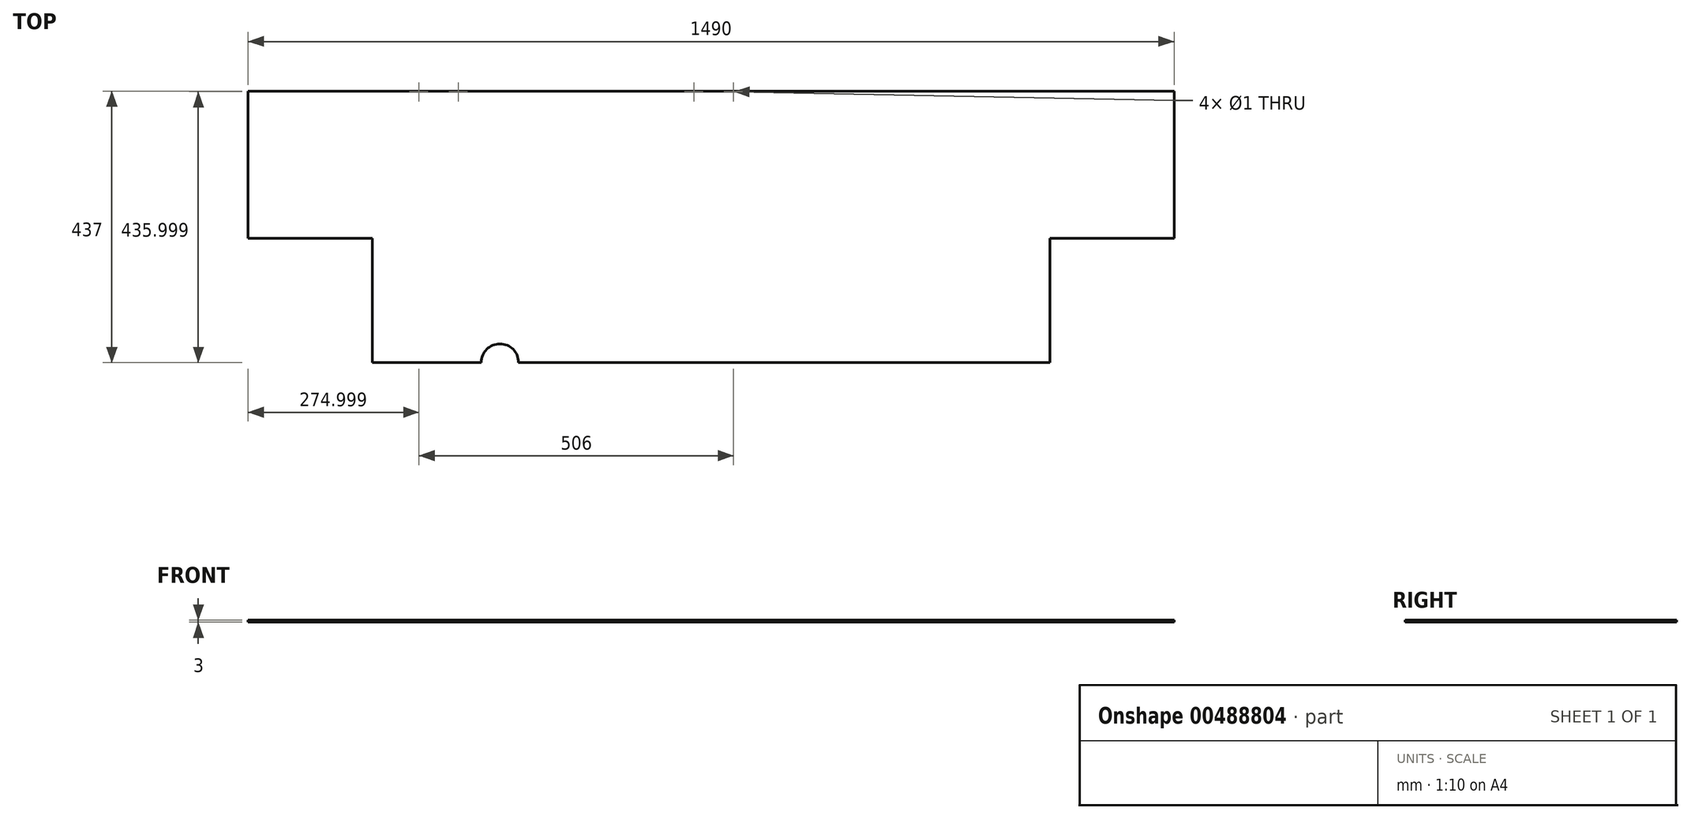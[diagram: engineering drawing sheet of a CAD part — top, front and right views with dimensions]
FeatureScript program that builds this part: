
annotation { "Feature Type Name" : "Feature", "Feature Type Description" : "" }
export const myFeature = defineFeature(function(context is Context, id is Id, definition is map)
    precondition{}
    {
        {
            var Q0;
            Q0=qCreatedBy(makeId("Top.planeOp"),FACE);
            var sketch = newSketch(context, id + "F0", { "sketchPlane" : qUnion([Q0])});
            skLineSegment(sketch, "E0.bottom", {"start": v(-755.66, 172.25) * mm, "end": v(734.34, 172.25) * mm});
            skLineSegment(sketch, "E0.top", {"start": v(-555.66, -264.75) * mm, "end": v(534.34, -264.75) * mm});
            skLineSegment(sketch, "E0.left", {"start": v(-755.66, 172.25) * mm, "end": v(-755.66, -64.75) * mm});
            skLineSegment(sketch, "E0.right", {"start": v(734.34, 172.25) * mm, "end": v(734.34, -64.75) * mm});
            skLineSegment(sketch, "E1.top", {"start": v(-755.66, -64.75) * mm, "end": v(-555.66, -64.75) * mm});
            skLineSegment(sketch, "E1.right", {"start": v(-555.66, -264.75) * mm, "end": v(-555.66, -64.75) * mm});
            skLineSegment(sketch, "E2.top", {"start": v(734.34, -64.75) * mm, "end": v(534.34, -64.75) * mm});
            skLineSegment(sketch, "E2.right", {"start": v(534.34, -264.75) * mm, "end": v(534.34, -64.75) * mm});
            skArc(sketch, "E3", {"start": v(-320.66, -264.75) * mm, "mid": v(-350.66, -234.75) * mm, "end": v(-380.66, -264.75) * mm});
            skLineSegment(sketch, "E4", {"start": v(-755.66, 172.25) * mm, "end": v(-480.66, 172.25) * mm});
            skLineSegment(sketch, "E5", {"start": v(-480.66, 172.25) * mm, "end": v(-402.51, 172.25) * mm});
            skLineSegment(sketch, "E6", {"start": v(-480.66, 172.25) * mm, "end": v(-417.16, 172.25) * mm});
            skLineSegment(sketch, "E7", {"start": v(-417.16, 172.25) * mm, "end": v(-38.16, 172.25) * mm});
            skLineSegment(sketch, "E8", {"start": v(-38.16, 172.25) * mm, "end": v(25.34, 172.25) * mm});
            skLineSegment(sketch, "E9", {"start": v(-480.66, 172.25) * mm, "end": v(-480.66, 170.81) * mm});
            skCircle(sketch, "E10", {"center": v(-480.66, 171.25) * mm, "radius": 0.5 * mm});
            skLineSegment(sketch, "E11", {"start": v(-417.16, 172.25) * mm, "end": v(-417.16, 170.25) * mm});
            skCircle(sketch, "E12", {"center": v(-417.16, 171.25) * mm, "radius": 0.5 * mm});
            skLineSegment(sketch, "E13", {"start": v(-38.16, 172.25) * mm, "end": v(-38.16, 169.8) * mm});
            skCircle(sketch, "E14", {"center": v(-38.16, 171.25) * mm, "radius": 0.5 * mm});
            skLineSegment(sketch, "E15", {"start": v(25.34, 172.25) * mm, "end": v(25.34, 170.25) * mm});
            skCircle(sketch, "E16", {"center": v(25.34, 171.25) * mm, "radius": 0.5 * mm});
            skSolve(sketch);
        }
        {
            var Q0;
            Q0=makeQuery(id+"F0.imprint","IMPRINT",FACE,{"disambiguationData":[TD([[makeQuery(id+"F0.imprint","IMPRINT",EDGE,{"derivedFrom":sQuery(id+"F0.wireOp",EDGE,"E0.bottom")}),-1.0]])]});
            extrude(context, id + "F1", {"entities" : qUnion([Q0]), "depth" : 3 * mm});
        }
        {
            var Q0;
            Q0 = qSketchRegion(id + "F0", true);
            extrude(context, id + "F2", {"entities" : qUnion([Q0]), "operationType" : NewBodyOperationType.REMOVE, "oppositeDirection" : true, "depth" : 25 * mm, "offsetDistance" : 25 * mm});
        }
        {
            var Q0;
            Q0 = qSketchRegion(id + "F0", true);
            extrude(context, id + "F3", {"entities" : qUnion([Q0]), "operationType" : NewBodyOperationType.REMOVE, "oppositeDirection" : true, "depth" : 25 * mm, "offsetDistance" : 25 * mm});
        }
    });
